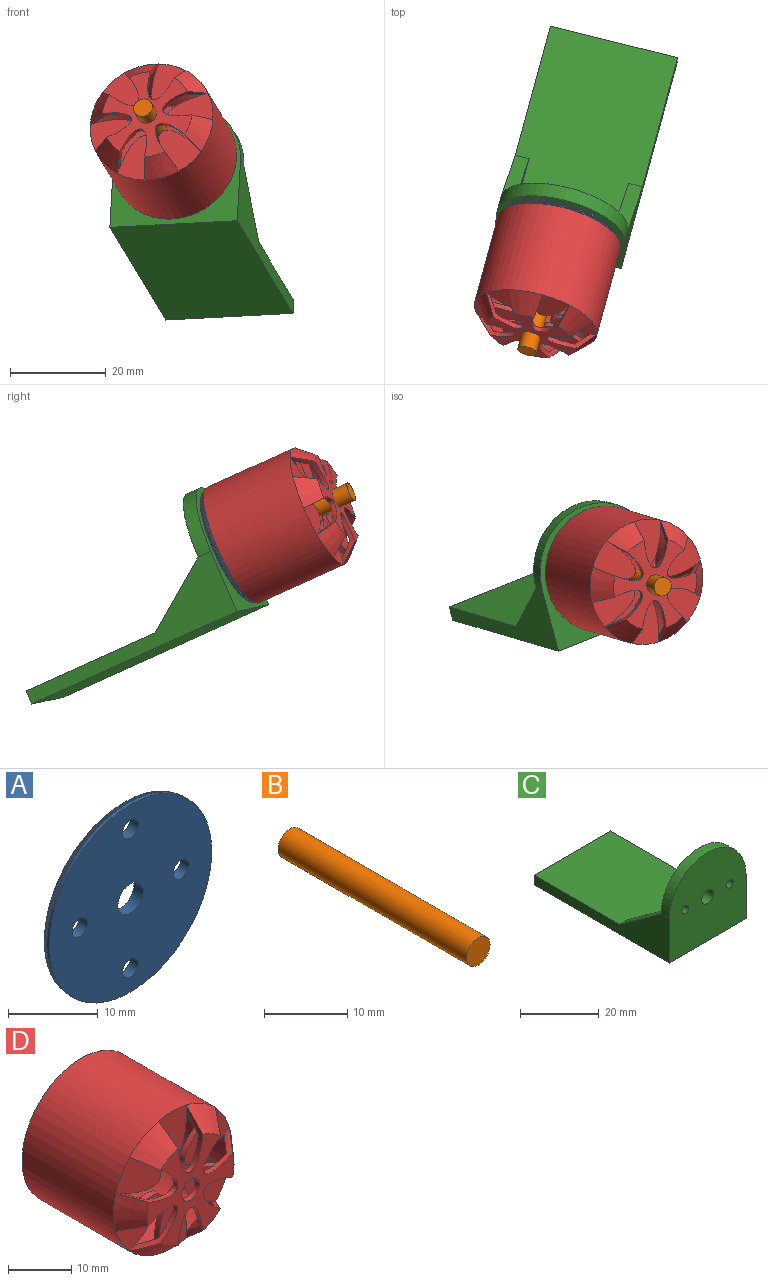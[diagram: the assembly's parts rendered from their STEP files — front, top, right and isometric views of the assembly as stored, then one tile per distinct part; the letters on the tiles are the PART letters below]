
ASSEMBLY  parts=4 mates=3
PART A: 13 faces, bbox 27.7x1.5x27.7 mm
  f0: plane 25.63x25.63mm, normal (0,-1,0), area 483.9mm2, adj f7,f8,f9,f10,f11,f12
  f1: cone r=12.25mm half-angle=89deg, axis (0,-1,0), area 439.2mm2, adj f2,f8,f9,f10,f11,f12
  f2: torus R=12.57mm, axis (0,1,0), area 38.9mm2, adj f1,f3
  f3: torus R=12.57mm, axis (0,1,0), area 23.9mm2, adj f2,f4
  f4: plane 25.52x25.52mm, normal (0,-1,0), area 30.8mm2, adj f3,f5
  f5: cylinder r=12.37mm len=24.74mm, axis (0,1,0), area 28.9mm2, adj f4,f6
  f6: plane 25.63x25.63mm, normal (0,1,0), area 35.4mm2, adj f5,f7
  f7: cylinder r=12.82mm len=25.63mm, axis (0,1,0), area 33.3mm2, adj f0,f6
  f8: cylinder r=2mm len=4mm, axis (0,-1,0), area 18.5mm2, adj f0,f1
  f9: cylinder r=1.25mm len=2.5mm, axis (0,-1,0), area 10.8mm2, adj f0,f1
  f10: cylinder r=1.25mm len=2.5mm, axis (0,-1,0), area 10.6mm2, adj f0,f1
  f11: cylinder r=1.25mm len=2.5mm, axis (0,-1,0), area 10.6mm2, adj f0,f1
  f12: cylinder r=1.25mm len=2.5mm, axis (0,-1,0), area 10.8mm2, adj f0,f1
PART B: 3 faces, bbox 4x32x4 mm
  f0: cylinder r=2mm len=32mm, axis (0,-1,0), area 402.1mm2, adj f1,f2
  f1: plane 4x4mm, normal (0,1,0), area 12.6mm2, adj f0
  f2: plane 4x4mm, normal (0,-1,0), area 12.6mm2, adj f0
PART C: 15 faces, bbox 27.5x48.6x27.5 mm
  f0: plane 48.58x13.75mm, normal (1,0,0), area 258.6mm2, adj f3,f5,f6,f8,f9,f14
  f1: plane 15x10.75mm, normal (-1,0,0), area 80.6mm2, adj f4,f8,f14
  f2: plane 15x10.75mm, normal (1,0,0), area 80.6mm2, adj f4,f8,f13
  f3: plane 27.5x27.5mm, normal (0,-1,0), area 651.1mm2, adj f0,f5,f6,f7,f10,f11,f12
  f4: plane 27.5x24.5mm, normal (0,1,0), area 504.1mm2, adj f1,f2,f6,f8,f10,f11,f12,f13
  f5: plane 48.58x27.5mm, normal (0,0,-1), area 1336mm2, adj f0,f3,f7,f9
  f6: cylinder r=13.75mm len=27.5mm, axis (0,1,0), area 129.6mm2, adj f0,f3,f4,f7
  f7: plane 48.58x13.75mm, normal (-1,0,0), area 258.6mm2, adj f3,f5,f6,f8,f9,f13
  f8: plane 45.58x27.5mm, normal (0,0,1), area 1163.5mm2, adj f0,f1,f2,f4,f7,f9,f13,f14
  f9: plane 27.5x3mm, normal (0,1,0), area 82.5mm2, adj f0,f5,f7,f8
  f10: cylinder r=2.12mm len=4.25mm, axis (0,-1,0), area 40.1mm2, adj f3,f4
  f11: cylinder r=1.25mm len=3mm, axis (0,-1,0), area 23.6mm2, adj f3,f4
  f12: cylinder r=1.25mm len=3mm, axis (0,-1,0), area 23.6mm2, adj f3,f4
  f13: plane 15x10.75mm, normal (0,0.58,0.81), area 55.4mm2, adj f2,f4,f7,f8
  f14: plane 15x10.75mm, normal (0,0.58,0.81), area 55.4mm2, adj f0,f1,f4,f8
PART D: 44 faces, bbox 26.5x24.5x26.5 mm
  f0: cone r=13.25mm half-angle=41.2deg, axis (0,1,0), area 31.9mm2, adj f6,f8,f18,f20
  f1: cone r=13.25mm half-angle=41.2deg, axis (0,1,0), area 31.9mm2, adj f6,f8,f12,f18
  f2: cone r=13.25mm half-angle=41.2deg, axis (0,1,0), area 31.9mm2, adj f6,f8,f14,f16
  f3: cone r=13.25mm half-angle=41.2deg, axis (0,1,0), area 31.9mm2, adj f6,f8,f14,f20
  f4: cone r=13.25mm half-angle=41.2deg, axis (0,1,0), area 31.9mm2, adj f6,f8,f10,f12
  f5: plane 26.5x26.5mm, normal (0,1,0), area 539mm2, adj f6,f43
  f6: cylinder r=13.25mm len=26.5mm, axis (0,-1,0), area 1706.7mm2, adj f0,f1,f2,f3,f4,f5,f7,f9
  f7: cone r=13.25mm half-angle=41.2deg, axis (0,1,0), area 31.9mm2, adj f6,f8,f10,f16
  f8: plane 19.5x18.69mm, normal (0,-1,0), area 133.4mm2, adj f0,f1,f2,f3,f4,f7,f10,f12
  f9: plane 10x6.28mm, normal (0,-1,0), area 50.4mm2, adj f6,f10,f31
  f10: bspline ~9.62x6.28mm, area 23mm2, adj f4,f7,f8,f9,f25,f28,f29
  f11: plane 10.07x8.32mm, normal (0,-1,0), area 50.4mm2, adj f6,f12,f33
  f12: bspline ~10.06x8.32mm, area 23mm2, adj f1,f4,f8,f11,f22,f25,f29
  f13: plane 10.07x8.32mm, normal (0,-1,0), area 50.4mm2, adj f6,f14,f35
  f14: bspline ~10.06x8.32mm, area 23mm2, adj f2,f3,f8,f13,f23,f24,f29
  f15: plane 10.07x8.32mm, normal (0,-1,0), area 50.4mm2, adj f6,f16,f37
  f16: bspline ~10.06x8.32mm, area 23mm2, adj f2,f7,f8,f15,f23,f28,f29
  f17: plane 10.07x8.32mm, normal (0,-1,0), area 50.4mm2, adj f6,f18,f39
  f18: bspline ~10.06x8.32mm, area 23mm2, adj f0,f1,f8,f17,f21,f22,f29
  f19: plane 10x6.28mm, normal (0,-1,0), area 50.4mm2, adj f6,f20,f41
  f20: bspline ~9.62x6.28mm, area 23mm2, adj f0,f3,f8,f19,f21,f24,f29
  f21: cone r=12.5mm half-angle=41.2deg, axis (0,1,0), area 23.4mm2, adj f18,f20,f27,f29,f39,f41
  f22: cone r=12.5mm half-angle=41.2deg, axis (0,1,0), area 23.4mm2, adj f12,f18,f27,f29,f33,f39
  f23: cone r=12.5mm half-angle=41.2deg, axis (0,1,0), area 23.4mm2, adj f14,f16,f27,f29,f35,f37
  f24: cone r=12.5mm half-angle=41.2deg, axis (0,1,0), area 23.4mm2, adj f14,f20,f27,f29,f35,f41
  f25: cone r=12.5mm half-angle=41.2deg, axis (0,1,0), area 23.4mm2, adj f10,f12,f27,f29,f31,f33
  f26: plane 24.5x24.5mm, normal (0,-1,0), area 458.9mm2, adj f27,f43
  f27: cylinder r=12.25mm len=24.5mm, axis (0,-1,0), area 1447.9mm2, adj f21,f22,f23,f24,f25,f26,f28,f30
  f28: cone r=12.5mm half-angle=41.2deg, axis (0,1,0), area 23.4mm2, adj f10,f16,f27,f29,f31,f37
  f29: plane 18.59x17.74mm, normal (0,1,0), area 117.4mm2, adj f10,f12,f14,f16,f18,f20,f21,f22
  f30: plane 9.05x6.39mm, normal (0,1,0), area 45mm2, adj f27,f31
  f31: bspline ~8.63x6.38mm, area 19.4mm2, adj f9,f25,f27,f28,f30
  f32: plane 9.25x7.9mm, normal (0,1,0), area 45mm2, adj f27,f33
  f33: bspline ~9.25x7.91mm, area 19.4mm2, adj f11,f22,f25,f27,f32
  f34: plane 9.25x7.9mm, normal (0,1,0), area 45.1mm2, adj f27,f35
  f35: bspline ~9.25x7.91mm, area 19.4mm2, adj f13,f23,f24,f27,f34
  f36: plane 9.25x7.9mm, normal (0,1,0), area 45.1mm2, adj f27,f37
  f37: bspline ~9.25x7.91mm, area 19.4mm2, adj f15,f23,f27,f28,f36
  f38: plane 9.25x7.9mm, normal (0,1,0), area 45mm2, adj f27,f39
  f39: bspline ~9.25x7.91mm, area 19.4mm2, adj f17,f21,f22,f27,f38
  f40: plane 9.05x6.39mm, normal (0,1,0), area 45.1mm2, adj f27,f41
  f41: bspline ~8.63x6.38mm, area 19.4mm2, adj f19,f21,f24,f27,f40
  f42: cylinder r=2mm len=4mm, axis (0,-1,0), area 12.6mm2, adj f8,f29
  f43: cylinder r=2mm len=4mm, axis (0,-1,0), area 12.6mm2, adj f5,f26
PLACE A rot(axis=(-0.86,0,-0.52),27.8deg) t=(-93.06,-62.58,-9.57)mm
PLACE B rot(axis=(0.98,-0.16,-0.15),158.7deg) t=(-85.36,-34.27,-22.34)mm
PLACE C rot(axis=(-0.86,0,-0.52),27.8deg) t=(-85.25,-33.84,-22.53)mm fixed
PLACE D rot(axis=(-0.66,0.52,-0.55),32.6deg) t=(-93.06,-62.58,-9.57)mm
MATE revolute A.f1 <-> D.f0  axis (-0.24,-0.88,0.4) through (-86.33,-37.8,-20.74)mm
MATE fastened B.f0 <-> D.f0  axis (0.24,0.88,-0.4) through (-93.06,-62.58,-9.57)mm
MATE fastened A.f1 <-> C.f6  axis (-0.24,-0.88,0.4) through (-85.97,-36.5,-21.33)mm
